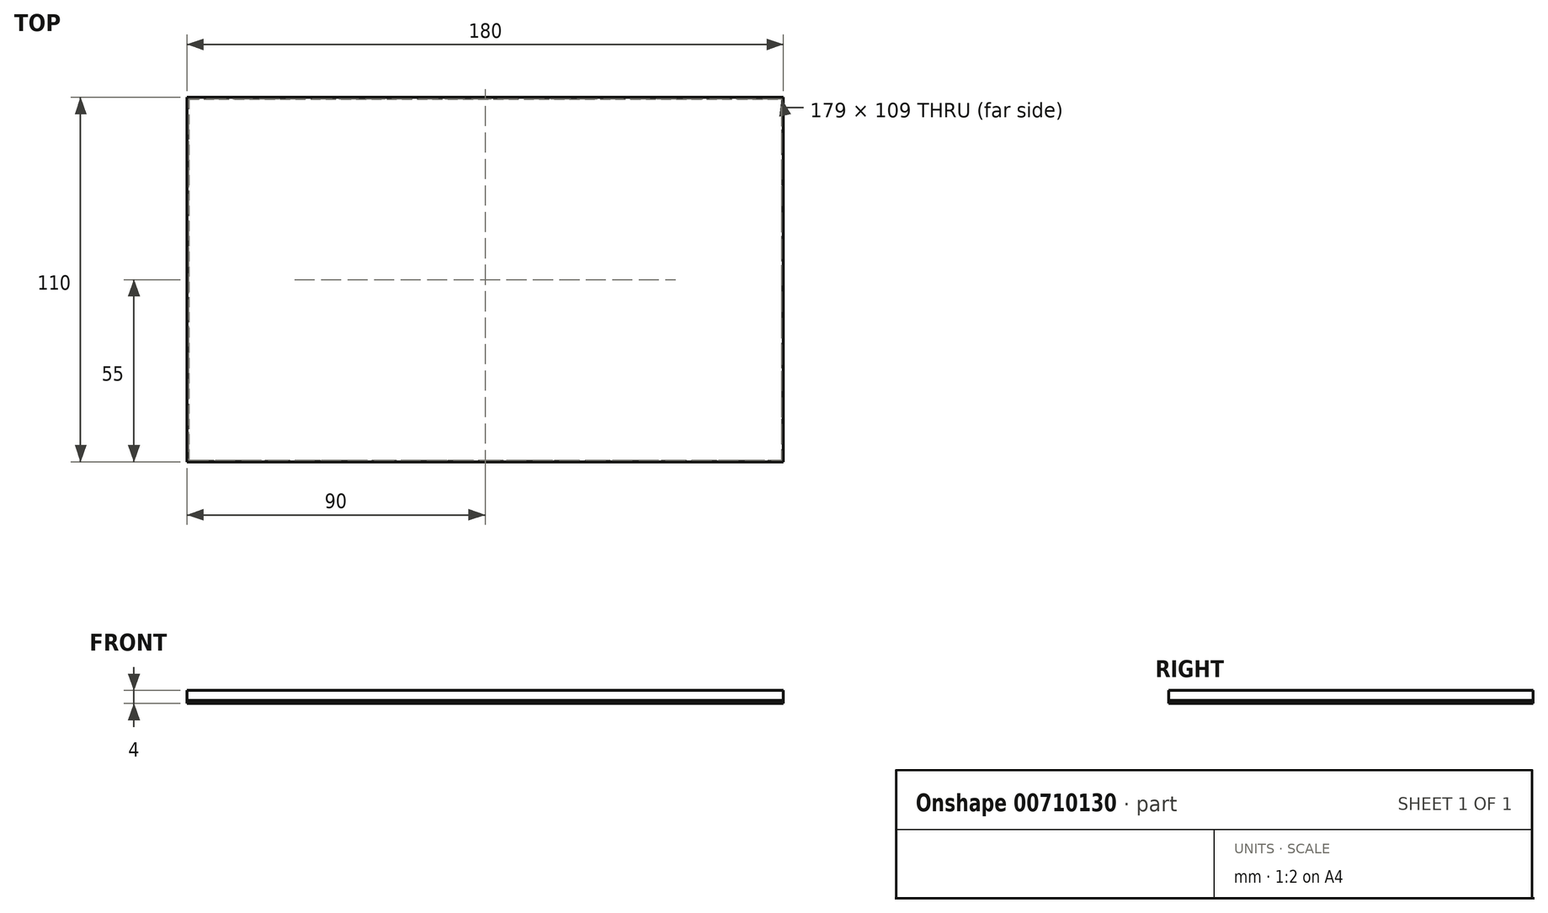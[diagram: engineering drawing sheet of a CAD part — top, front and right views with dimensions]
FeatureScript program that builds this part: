
annotation { "Feature Type Name" : "Feature", "Feature Type Description" : "" }
export const myFeature = defineFeature(function(context is Context, id is Id, definition is map)
    precondition{}
    {
        {
            var Q0;
            Q0=qCreatedBy(makeId("Top.planeOp"),FACE);
            var sketch = newSketch(context, id + "F0", { "sketchPlane" : qUnion([Q0])});
            skLineSegment(sketch, "E0.bottom", {"start": v(-90, 55) * mm, "end": v(90, 55) * mm});
            skLineSegment(sketch, "E0.top", {"start": v(-90, -55) * mm, "end": v(90, -55) * mm});
            skLineSegment(sketch, "E0.left", {"start": v(-90, 55) * mm, "end": v(-90, -55) * mm});
            skLineSegment(sketch, "E0.right", {"start": v(90, 55) * mm, "end": v(90, -55) * mm});
            skPoint(sketch, "E0.middle", {"position": v(0, 0) * mm});
            skSolve(sketch);
        }
        {
            var Q0;
            Q0=makeQuery(id+"F0.imprint","IMPRINT",FACE,{"disambiguationData":[TD([[makeQuery(id+"F0.imprint","IMPRINT",EDGE,{"derivedFrom":sQuery(id+"F0.wireOp",EDGE,"E0.bottom")}),-1.0]])]});
            extrude(context, id + "F1", {"entities" : qUnion([Q0]), "depth" : 3 * mm, "offsetDistance" : 25 * mm});
        }
        {
            var Q0;
            Q0=makeQuery(id+"F1.opExtrude","CAP_FACE",FACE,{"disambiguationData":[OSD([sQuery(id+"F0.wireOp",EDGE,"E0.bottom"),sQuery(id+"F0.wireOp",EDGE,"E0.top"),sQuery(id+"F0.wireOp",EDGE,"E0.left"),sQuery(id+"F0.wireOp",EDGE,"E0.right")])],"isStart":true});
            var sketch = newSketch(context, id + "F2", { "sketchPlane" : qUnion([Q0])});
            skLineSegment(sketch, "E1.bottom", {"start": v(-89.5, -54.5) * mm, "end": v(89.5, -54.5) * mm});
            skLineSegment(sketch, "E1.top", {"start": v(-89.5, 54.5) * mm, "end": v(89.5, 54.5) * mm});
            skLineSegment(sketch, "E1.left", {"start": v(-89.5, -54.5) * mm, "end": v(-89.5, 54.5) * mm});
            skLineSegment(sketch, "E1.right", {"start": v(89.5, -54.5) * mm, "end": v(89.5, 54.5) * mm});
            skPoint(sketch, "E1.middle", {"position": v(0, 0) * mm});
            skLineSegment(sketch, "E2.bottom", {"start": v(-90, -55) * mm, "end": v(90, -55) * mm});
            skLineSegment(sketch, "E2.top", {"start": v(-90, 55) * mm, "end": v(90, 55) * mm});
            skLineSegment(sketch, "E2.left", {"start": v(-90, -55) * mm, "end": v(-90, 55) * mm});
            skLineSegment(sketch, "E2.right", {"start": v(90, -55) * mm, "end": v(90, 55) * mm});
            skSolve(sketch);
        }
        {
            var Q0;
            Q0 = qSketchRegion(id + "F2", true);
            extrude(context, id + "F3", {"entities" : qUnion([Q0]), "depth" : 1 * mm, "offsetDistance" : 25 * mm});
        }
    });
